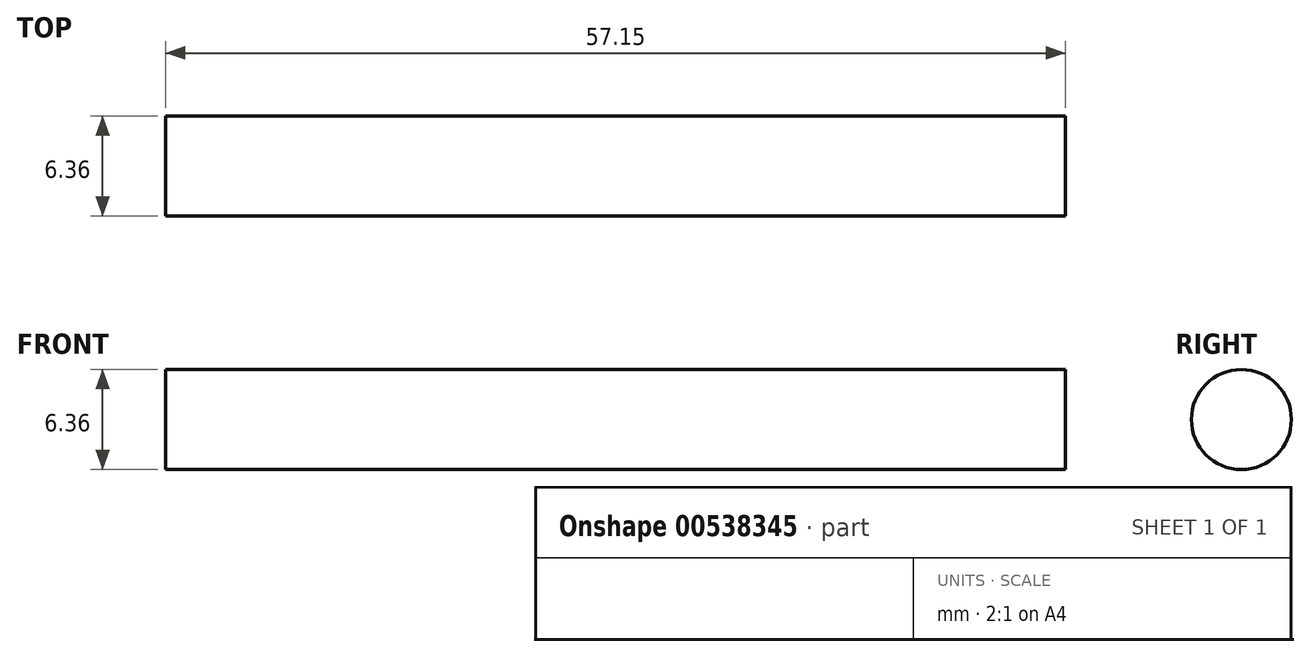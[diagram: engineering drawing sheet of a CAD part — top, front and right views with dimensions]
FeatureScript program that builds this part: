
annotation { "Feature Type Name" : "Feature", "Feature Type Description" : "" }
export const myFeature = defineFeature(function(context is Context, id is Id, definition is map)
    precondition{}
    {
        {
            var Q0;
            Q0=qCreatedBy(makeId("Right.planeOp"),FACE);
            var sketch = newSketch(context, id + "F0", { "sketchPlane" : qUnion([Q0])});
            skCircle(sketch, "E0", {"center": v(0, 0) * mm, "radius": 3.18 * mm});
            skSolve(sketch);
        }
        {
            var Q0;
            Q0 = qSketchRegion(id + "F0", true);
            extrude(context, id + "F1", {"entities" : qUnion([Q0]), "depth" : 57.15 * mm, "offsetDistance" : 25.4 * mm});
        }
    });
